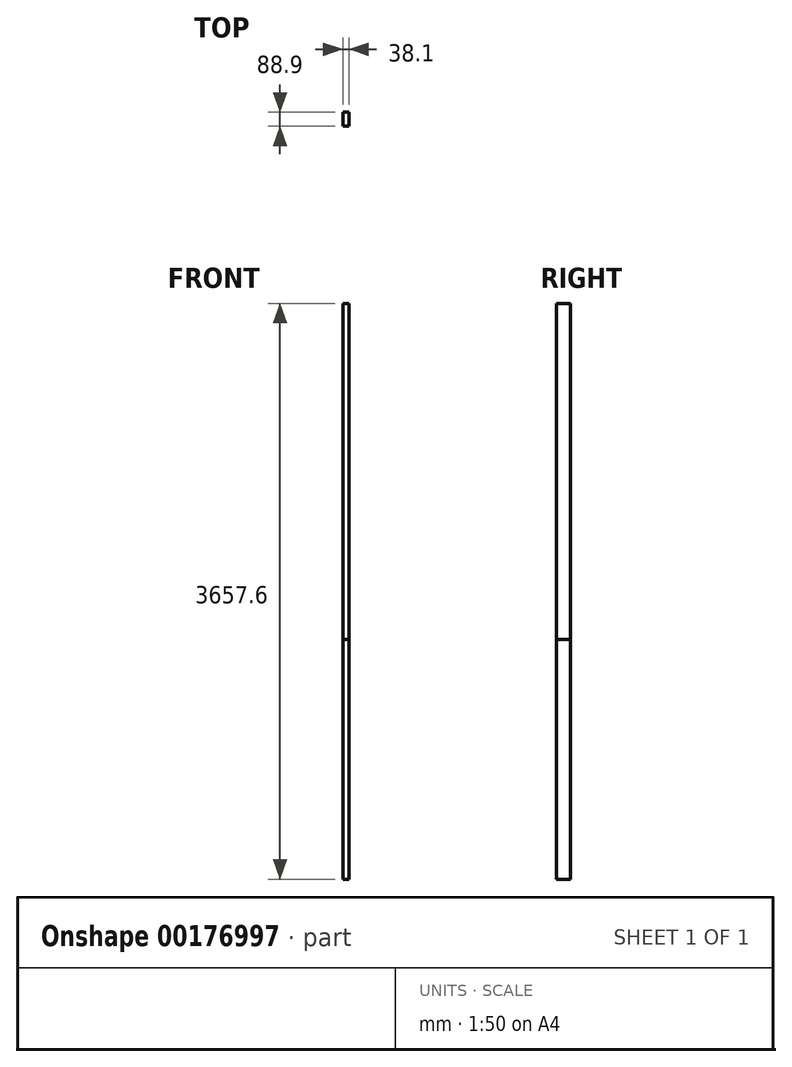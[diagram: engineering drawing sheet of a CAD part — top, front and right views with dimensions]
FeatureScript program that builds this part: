
annotation { "Feature Type Name" : "Feature", "Feature Type Description" : "" }
export const myFeature = defineFeature(function(context is Context, id is Id, definition is map)
    precondition{}
    {
        {
            var Q0;
            Q0=qCreatedBy(makeId("Top.planeOp"),FACE);
            var sketch = newSketch(context, id + "F0", { "sketchPlane" : qUnion([Q0])});
            skLineSegment(sketch, "E0.bottom", {"start": v(0, 0) * mm, "end": v(38.1, 0) * mm});
            skLineSegment(sketch, "E0.top", {"start": v(0, 88.9) * mm, "end": v(38.1, 88.9) * mm});
            skLineSegment(sketch, "E0.left", {"start": v(0, 0) * mm, "end": v(0, 88.9) * mm});
            skLineSegment(sketch, "E0.right", {"start": v(38.1, 0) * mm, "end": v(38.1, 88.9) * mm});
            skSolve(sketch);
        }
        {
            var Q0;
            Q0 = qSketchRegion(id + "F0", true);
            extrude(context, id + "F1", {"entities" : qUnion([Q0]), "depth" : 1524 * mm});
        }
        {
            var Q0;
            Q0 = qSketchRegion(id + "F0", true);
            extrude(context, id + "F2", {"entities" : qUnion([Q0]), "depth" : 3657.6 * mm});
        }
    });
